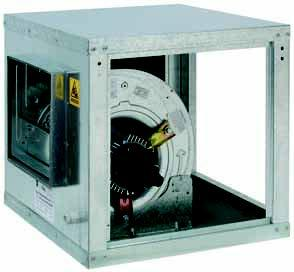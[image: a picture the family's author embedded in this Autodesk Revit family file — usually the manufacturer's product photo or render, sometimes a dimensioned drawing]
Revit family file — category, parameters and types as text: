
# Revit family: BD-ERP_25-25-M6
name_source: partatom
category: Aparatos eléctricos
revit_build: Autodesk Revit 2016 (Build: 20150220_1215(x64)
units: mm (PartAtom-declared; Revit-internal decimal feet)

## family parameters
Compartido = No
Corte con vacíos al cargar = No
Cota de conector redondo = Diámetro de uso
Mantener orientación de anotación = No
Número OmniClass = 23.80.00.00
Punto de cálculo de habitación = No
Se basa en plano de trabajo = No
Siempre vertical = Sí
Tipo de pieza = Caja de conexiones
Título OmniClass = Electric Power and Lighting

## types (1)
- BD ERP
    Caudal máx. = 1900 m3/h
    Clase = F
    Costo = 0 $
    Código de montaje = CV01623
    Descripción = CAJAS DE VENTILACIÓN CON MOTOR INCORPORADO
    Dimensiones exteriores = 500 x 490 x 490 mm
    Dimensiones ventana = Ø350 mm
    Fabricante = SALVADOR ESCODA
    Imagen de tipo = CajasVentilacion-BD-ERP.jpg
    Intensidad abs. monof. 50Hz-230V = 0,77 A
    Modelo = BD ERP 25/25 M6 CIRCULAR
    Nivel presión sonora = 54 db(A)
    Peso = 20 Kg
    Potencia motor = 0,12 kW
    Protección = IP-55
    URL = www.salvadorescoda.com
    Velocidad = 925 rpm
